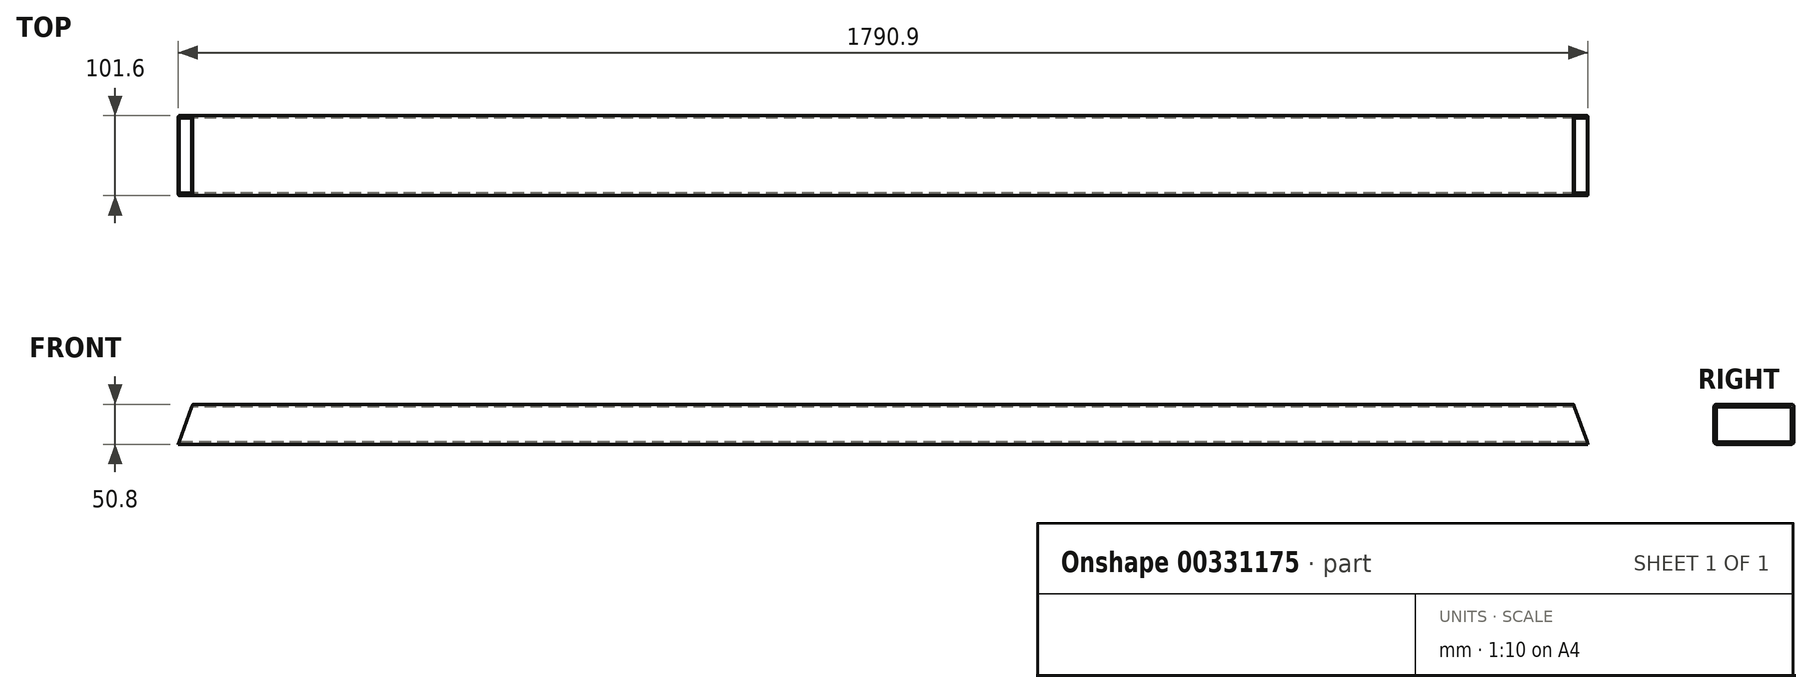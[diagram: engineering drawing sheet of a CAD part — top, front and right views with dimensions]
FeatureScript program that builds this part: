
annotation { "Feature Type Name" : "Feature", "Feature Type Description" : "" }
export const myFeature = defineFeature(function(context is Context, id is Id, definition is map)
    precondition{}
    {
        {
            var Q0;
            Q0=qCreatedBy(makeId("Right.planeOp"),FACE);
            var sketch = newSketch(context, id + "F0", { "sketchPlane" : qUnion([Q0])});
            skLineSegment(sketch, "E0.bottom", {"start": v(47.63, 25.4) * mm, "end": v(-47.62, 25.4) * mm});
            skLineSegment(sketch, "E0.top", {"start": v(47.63, -25.4) * mm, "end": v(-47.62, -25.4) * mm});
            skLineSegment(sketch, "E0.left", {"start": v(50.8, 22.23) * mm, "end": v(50.8, -22.23) * mm});
            skLineSegment(sketch, "E0.right", {"start": v(-50.8, 22.22) * mm, "end": v(-50.8, -22.23) * mm});
            skPoint(sketch, "E0.middle", {"position": v(0, 0) * mm});
            skPoint(sketch, "E1.visualSharp", {"position": v(-50.8, 25.4) * mm});
            skArc(sketch, "E1.filletArc", {"start": v(-47.63, 25.4) * mm, "mid": v(-49.87, 24.47) * mm, "end": v(-50.8, 22.22) * mm});
            skPoint(sketch, "E2.visualSharp", {"position": v(50.8, 25.4) * mm});
            skArc(sketch, "E2.filletArc", {"start": v(50.8, 22.23) * mm, "mid": v(49.87, 24.47) * mm, "end": v(47.63, 25.4) * mm});
            skPoint(sketch, "E3.visualSharp", {"position": v(-50.8, -25.4) * mm});
            skArc(sketch, "E3.filletArc", {"start": v(-50.8, -22.23) * mm, "mid": v(-49.87, -24.47) * mm, "end": v(-47.62, -25.4) * mm});
            skPoint(sketch, "E4.visualSharp", {"position": v(50.8, -25.4) * mm});
            skArc(sketch, "E4.filletArc", {"start": v(47.63, -25.4) * mm, "mid": v(49.87, -24.47) * mm, "end": v(50.8, -22.23) * mm});
            skLineSegment(sketch, "E5.0", {"start": v(47.62, 22.23) * mm, "end": v(-47.62, 22.23) * mm});
            skLineSegment(sketch, "E5.1", {"start": v(47.62, 22.23) * mm, "end": v(47.63, -22.23) * mm});
            skLineSegment(sketch, "E5.2", {"start": v(47.63, -22.23) * mm, "end": v(-47.62, -22.23) * mm});
            skLineSegment(sketch, "E5.3", {"start": v(-47.62, 22.23) * mm, "end": v(-47.62, -22.23) * mm});
            skSolve(sketch);
        }
        {
            var Q0;
            Q0 = qSketchRegion(id + "F0", true);
            extrude(context, id + "F1", {"entities" : qUnion([Q0]), "depth" : 1790.9 * mm});
        }
        {
            var Q0;
            Q0=makeQuery(id+"F1.opExtrude","SWEPT_FACE",FACE,{"disambiguationData":[OSD([sQuery(id+"F0.wireOp",EDGE,"E0.right")])]});
            var sketch = newSketch(context, id + "F2", { "sketchPlane" : qUnion([Q0])});
            skLineSegment(sketch, "E6.bottom", {"start": v(18.49, 25.4) * mm, "end": v(0, 25.4) * mm});
            skLineSegment(sketch, "E6.right", {"start": v(0, 25.4) * mm, "end": v(0, -25.4) * mm});
            skPoint(sketch, "E6.middle", {"position": v(9.24, 0) * mm});
            skLineSegment(sketch, "E7", {"start": v(0, -25.4) * mm, "end": v(18.49, 25.4) * mm});
            skPoint(sketch, "E6.top.start.orphan", {"position": v(18.49, -25.4) * mm});
            skLineSegment(sketch, "E8.bottom", {"start": v(1790.9, 25.4) * mm, "end": v(1772.41, 25.4) * mm});
            skLineSegment(sketch, "E8.left", {"start": v(1790.9, 25.4) * mm, "end": v(1790.9, -25.4) * mm});
            skPoint(sketch, "E8.middle", {"position": v(1781.66, 0) * mm});
            skLineSegment(sketch, "E9", {"start": v(1772.41, 25.4) * mm, "end": v(1790.9, -25.4) * mm});
            skPoint(sketch, "E8.top.end.orphan", {"position": v(1772.41, -25.4) * mm});
            skSolve(sketch);
        }
        {
            var Q0;
            Q0 = qSketchRegion(id + "F2", true);
            extrude(context, id + "F3", {"entities" : qUnion([Q0]), "operationType" : NewBodyOperationType.REMOVE, "endBound" : BoundingType.THROUGH_ALL, "oppositeDirection" : true, "depth" : 25.4 * mm});
        }
    });
